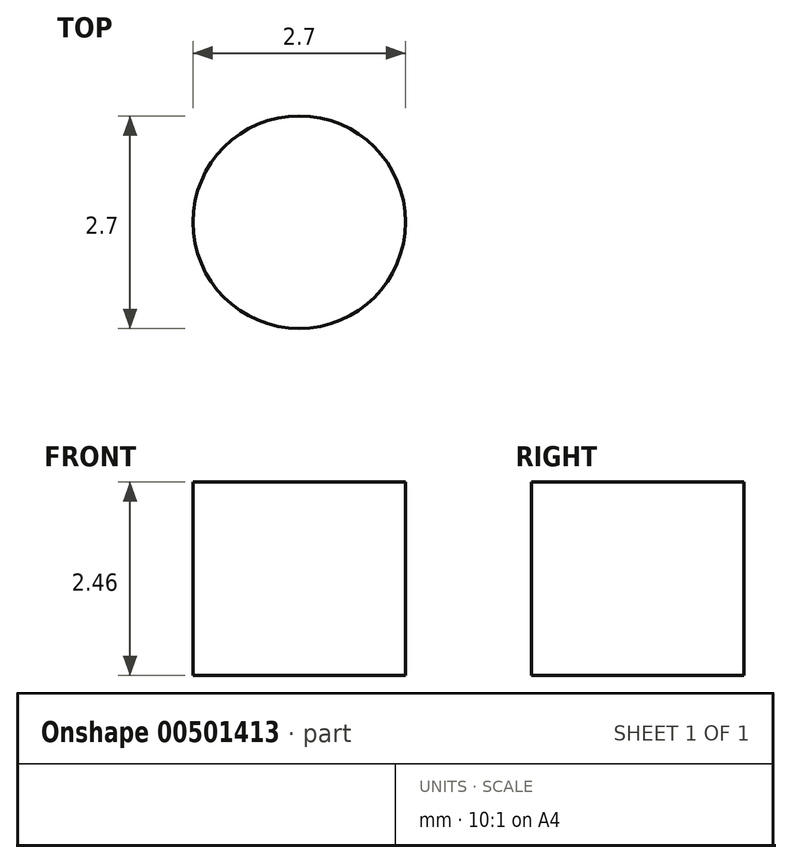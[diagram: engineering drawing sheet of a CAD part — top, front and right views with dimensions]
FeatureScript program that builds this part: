
annotation { "Feature Type Name" : "Feature", "Feature Type Description" : "" }
export const myFeature = defineFeature(function(context is Context, id is Id, definition is map)
    precondition{}
    {
        {
            var Q0;
            Q0=qCreatedBy(makeId("Top.planeOp"),FACE);
            var sketch = newSketch(context, id + "F0", { "sketchPlane" : qUnion([Q0])});
            skLineSegment(sketch, "E0", {"start": v(-3.35, 0) * mm, "end": v(3.63, 0) * mm, "construction": true});
            skLineSegment(sketch, "E1", {"start": v(0, 4.04) * mm, "end": v(0, -2.89) * mm, "construction": true});
            skCircle(sketch, "E2", {"center": v(0, 0) * mm, "radius": 1.35 * mm});
            skSolve(sketch);
        }
        {
            var Q0;
            Q0=makeQuery(id+"F0.imprint","IMPRINT",FACE,{"disambiguationData":[TD([[makeQuery(id+"F0.imprint","IMPRINT",EDGE,{"derivedFrom":sQuery(id+"F0.wireOp",EDGE,"E2")}),1.0]])]});
            extrude(context, id + "F1", {"entities" : qUnion([Q0]), "depth" : 2.46 * mm, "offsetDistance" : 25 * mm});
        }
    });
